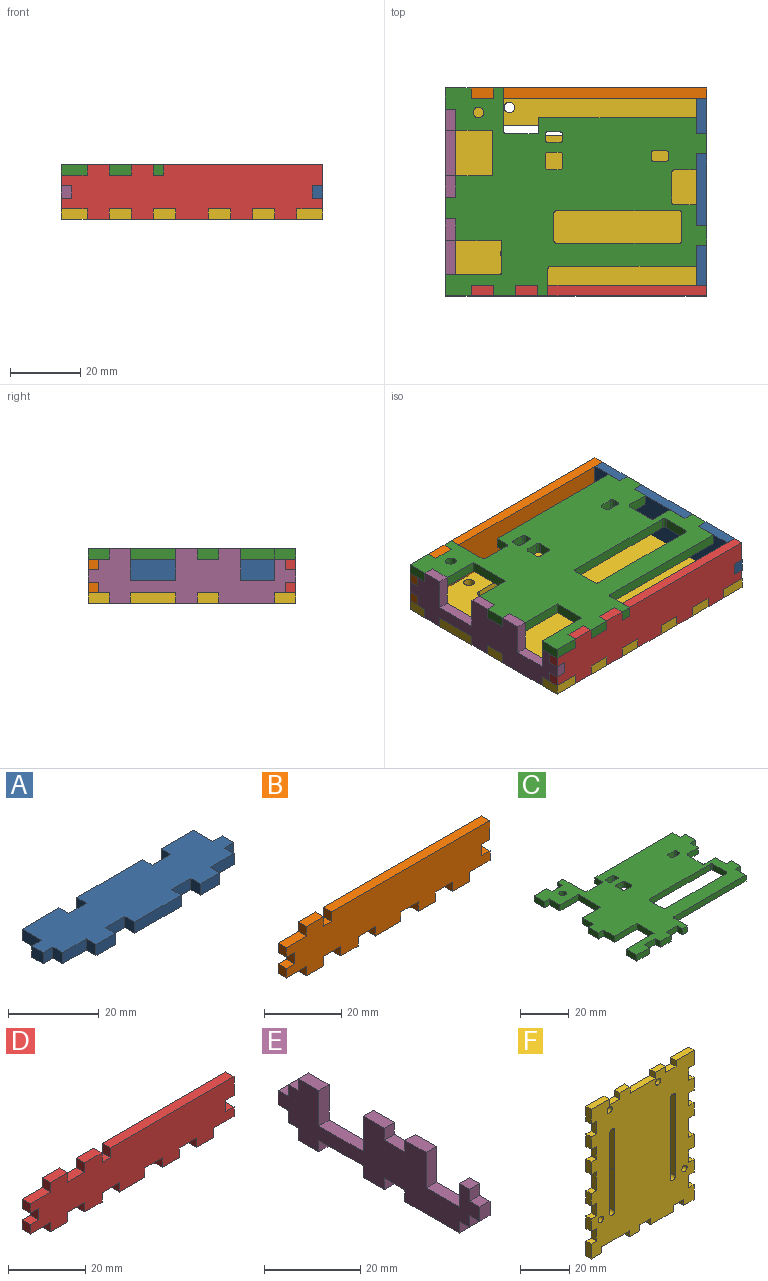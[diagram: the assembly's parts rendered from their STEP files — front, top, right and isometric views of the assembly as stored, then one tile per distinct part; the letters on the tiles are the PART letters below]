
ASSEMBLY  parts=6 mates=5
PART A: 34 faces, bbox 59.3x15.6x3 mm
  f0: plane 11.5x3mm, normal (0,1,0), area 34.5mm2, adj f1,f31,f32,f33
  f1: plane 6x3mm, normal (-1,0,0), area 18mm2, adj f0,f2,f32,f33
  f2: plane 3x3mm, normal (0,1,0), area 9mm2, adj f1,f3,f32,f33
  f3: plane 3.6x3mm, normal (-1,0,0), area 10.8mm2, adj f2,f4,f32,f33
  f4: plane 3x3mm, normal (0,-1,0), area 9mm2, adj f3,f5,f32,f33
  f5: plane 3x3mm, normal (-1,0,0), area 9mm2, adj f4,f6,f32,f33
  f6: plane 7.4x3mm, normal (0,-1,0), area 22.2mm2, adj f5,f7,f32,f33
  f7: plane 3x3mm, normal (-1,0,0), area 9mm2, adj f6,f8,f32,f33
  f8: plane 6x3mm, normal (0,-1,0), area 18mm2, adj f7,f9,f32,f33
  f9: plane 3x3mm, normal (1,0,0), area 9mm2, adj f8,f10,f32,f33
  f10: plane 6x3mm, normal (0,-1,0), area 18mm2, adj f9,f11,f32,f33
  f11: plane 3x3mm, normal (-1,0,0), area 9mm2, adj f10,f12,f32,f33
  f12: plane 14.5x3mm, normal (0,-1,0), area 43.5mm2, adj f11,f13,f32,f33
  f13: plane 3x3mm, normal (1,0,0), area 9mm2, adj f12,f14,f32,f33
  f14: plane 6x3mm, normal (0,-1,0), area 18mm2, adj f13,f15,f32,f33
  f15: plane 3x3mm, normal (-1,0,0), area 9mm2, adj f14,f16,f32,f33
  f16: plane 6x3mm, normal (0,-1,0), area 18mm2, adj f15,f17,f32,f33
  f17: plane 3x3mm, normal (1,0,0), area 9mm2, adj f16,f18,f32,f33
  f18: plane 7.4x3mm, normal (0,-1,0), area 22.2mm2, adj f17,f19,f32,f33
  f19: plane 3x3mm, normal (1,0,0), area 9mm2, adj f18,f20,f32,f33
  f20: plane 3x3mm, normal (0,-1,0), area 9mm2, adj f19,f21,f32,f33
  f21: plane 3.6x3mm, normal (1,0,0), area 10.8mm2, adj f20,f22,f32,f33
  f22: plane 3x3mm, normal (0,1,0), area 9mm2, adj f21,f23,f32,f33
  f23: plane 6x3mm, normal (1,0,0), area 18mm2, adj f22,f24,f32,f33
  f24: plane 10x3mm, normal (0,1,0), area 30mm2, adj f23,f25,f32,f33
  f25: plane 3x3mm, normal (-1,0,0), area 9mm2, adj f24,f26,f32,f33
  f26: plane 5.8x3mm, normal (0,1,0), area 17.4mm2, adj f25,f27,f32,f33
  f27: plane 3x3mm, normal (1,0,0), area 9mm2, adj f26,f28,f32,f33
  f28: plane 20.5x3mm, normal (0,1,0), area 61.5mm2, adj f27,f29,f32,f33
  f29: plane 3x3mm, normal (-1,0,0), area 9mm2, adj f28,f30,f32,f33
  f30: plane 5.5x3mm, normal (0,1,0), area 16.5mm2, adj f29,f31,f32,f33
  f31: plane 3x3mm, normal (1,0,0), area 9mm2, adj f0,f30,f32,f33
  f32: plane 59.3x15.6mm, normal (0,0,-1), area 738.8mm2, adj f0,f1,f2,f3,f4,f5,f6,f7
  f33: plane 59.3x15.6mm, normal (0,0,1), area 738.8mm2, adj f0,f1,f2,f3,f4,f5,f6,f7
PART B: 40 faces, bbox 74.6x3x15.6 mm
  f0: plane 3x3mm, normal (0,0,-1), area 9mm2, adj f1,f37,f38,f39
  f1: plane 6x3mm, normal (1,0,0), area 18mm2, adj f0,f2,f38,f39
  f2: plane 57.9x3mm, normal (0,0,1), area 173.7mm2, adj f1,f3,f38,f39
  f3: plane 3x3mm, normal (-1,0,0), area 9mm2, adj f2,f4,f38,f39
  f4: plane 3x3mm, normal (0,0,1), area 9mm2, adj f3,f5,f38,f39
  f5: plane 3x3mm, normal (1,0,0), area 9mm2, adj f4,f6,f38,f39
  f6: plane 6.3x3mm, normal (0,0,1), area 18.9mm2, adj f5,f7,f38,f39
  f7: plane 3x3mm, normal (-1,0,0), area 9mm2, adj f6,f8,f38,f39
  f8: plane 7.4x3mm, normal (0,0,1), area 22.2mm2, adj f7,f9,f38,f39
  f9: plane 3x3mm, normal (-1,0,0), area 9mm2, adj f8,f10,f38,f39
  f10: plane 3x3mm, normal (0,0,-1), area 9mm2, adj f9,f11,f38,f39
  f11: plane 3.6x3mm, normal (-1,0,0), area 10.8mm2, adj f10,f12,f38,f39
  f12: plane 3x3mm, normal (0,0,1), area 9mm2, adj f11,f13,f38,f39
  f13: plane 3x3mm, normal (-1,0,0), area 9mm2, adj f12,f14,f38,f39
  f14: plane 7.4x3mm, normal (0,0,-1), area 22.2mm2, adj f13,f15,f38,f39
  f15: plane 3x3mm, normal (-1,0,0), area 9mm2, adj f14,f16,f38,f39
  f16: plane 6.3x3mm, normal (0,0,-1), area 18.9mm2, adj f15,f17,f38,f39
  f17: plane 3x3mm, normal (1,0,0), area 9mm2, adj f16,f18,f38,f39
  f18: plane 6.3x3mm, normal (0,0,-1), area 18.9mm2, adj f17,f19,f38,f39
  f19: plane 3x3mm, normal (-1,0,0), area 9mm2, adj f18,f20,f38,f39
  f20: plane 6.3x3mm, normal (0,0,-1), area 18.9mm2, adj f19,f21,f38,f39
  f21: plane 3x3mm, normal (1,0,0), area 9mm2, adj f20,f22,f38,f39
  f22: plane 6.3x3mm, normal (0,0,-1), area 18.9mm2, adj f21,f23,f38,f39
  f23: plane 3x3mm, normal (-1,0,0), area 9mm2, adj f22,f24,f38,f39
  f24: plane 9.4x3mm, normal (0,0,-1), area 28.2mm2, adj f23,f25,f38,f39
  f25: plane 3x3mm, normal (1,0,0), area 9mm2, adj f24,f26,f38,f39
  f26: plane 6.3x3mm, normal (0,0,-1), area 18.9mm2, adj f25,f27,f38,f39
  f27: plane 3x3mm, normal (-1,0,0), area 9mm2, adj f26,f28,f38,f39
  f28: plane 6.3x3mm, normal (0,0,-1), area 18.9mm2, adj f27,f29,f38,f39
  f29: plane 3x3mm, normal (1,0,0), area 9mm2, adj f28,f30,f38,f39
  f30: plane 6.3x3mm, normal (0,0,-1), area 18.9mm2, adj f29,f31,f38,f39
  f31: plane 3x3mm, normal (-1,0,0), area 9mm2, adj f30,f32,f38,f39
  f32: plane 6.3x3mm, normal (0,0,-1), area 18.9mm2, adj f31,f33,f38,f39
  f33: plane 3x3mm, normal (1,0,0), area 9mm2, adj f32,f34,f38,f39
  f34: plane 7.4x3mm, normal (0,0,-1), area 22.2mm2, adj f33,f35,f38,f39
  f35: plane 3x3mm, normal (1,0,0), area 9mm2, adj f34,f36,f38,f39
  f36: plane 3x3mm, normal (0,0,1), area 9mm2, adj f35,f37,f38,f39
  f37: plane 3.6x3mm, normal (1,0,0), area 10.8mm2, adj f0,f36,f38,f39
  f38: plane 74.6x15.6mm, normal (0,-1,0), area 991mm2, adj f0,f1,f2,f3,f4,f5,f6,f7
  f39: plane 74.6x15.6mm, normal (0,1,0), area 991mm2, adj f0,f1,f2,f3,f4,f5,f6,f7
PART C: 88 faces, bbox 74.6x59.3x3 mm
  f0: plane 3x3mm, normal (0,1,0), area 9mm2, adj f1,f85,f86,f87
  f1: plane 6x3mm, normal (1,0,0), area 18mm2, adj f0,f2,f86,f87
  f2: plane 6.25x3mm, normal (0,1,0), area 18.7mm2, adj f1,f3,f86,f87
  f3: cylinder r=0.75mm len=3mm, axis (0,0,1), area 3.5mm2, adj f2,f4,f86,f87
  f4: plane 8.5x3mm, normal (1,0,0), area 25.5mm2, adj f3,f5,f86,f87
  f5: cylinder r=0.75mm len=3mm, axis (0,0,1), area 3.5mm2, adj f4,f6,f86,f87
  f6: plane 6.25x3mm, normal (0,-1,0), area 18.7mm2, adj f5,f7,f86,f87
  f7: plane 4.5x3mm, normal (1,0,0), area 13.5mm2, adj f6,f8,f86,f87
  f8: plane 3x3mm, normal (0,-1,0), area 9mm2, adj f7,f9,f86,f87
  f9: plane 5.8x3mm, normal (1,0,0), area 17.4mm2, adj f8,f10,f86,f87
  f10: plane 3x3mm, normal (0,1,0), area 9mm2, adj f9,f11,f86,f87
  f11: plane 4.5x3mm, normal (1,0,0), area 13.5mm2, adj f10,f12,f86,f87
  f12: plane 44.9x3mm, normal (0,1,0), area 134.7mm2, adj f11,f13,f86,f87
  f13: plane 3.85x3mm, normal (-1,0,0), area 11.5mm2, adj f12,f14,f86,f87
  f14: cylinder r=0.75mm len=3mm, axis (0,0,1), area 3.5mm2, adj f13,f15,f86,f87
  f15: plane 8.5x3mm, normal (0,1,0), area 25.5mm2, adj f14,f16,f86,f87
  f16: cylinder r=0.75mm len=3mm, axis (0,0,1), area 3.5mm2, adj f15,f17,f86,f87
  f17: plane 12.35x3mm, normal (1,0,0), area 37mm2, adj f16,f18,f86,f87
  f18: plane 3x3mm, normal (0,1,0), area 9mm2, adj f17,f19,f86,f87
  f19: plane 3x3mm, normal (-1,0,0), area 9mm2, adj f18,f20,f86,f87
  f20: plane 6.3x3mm, normal (0,1,0), area 18.9mm2, adj f19,f21,f86,f87
  f21: plane 3x3mm, normal (1,0,0), area 9mm2, adj f20,f22,f86,f87
  f22: plane 7.4x3mm, normal (0,1,0), area 22.2mm2, adj f21,f23,f86,f87
  f23: plane 6x3mm, normal (-1,0,0), area 18mm2, adj f22,f24,f86,f87
  f24: plane 3x3mm, normal (0,-1,0), area 9mm2, adj f23,f25,f86,f87
  f25: plane 6x3mm, normal (-1,0,0), area 18mm2, adj f24,f26,f86,f87
  f26: plane 10.5x3mm, normal (0,-1,0), area 31.5mm2, adj f25,f27,f86,f87
  f27: plane 13x3mm, normal (-1,0,0), area 39mm2, adj f26,f28,f86,f87
  f28: plane 10.5x3mm, normal (0,1,0), area 31.5mm2, adj f27,f29,f86,f87
  f29: plane 6.2x3mm, normal (-1,0,0), area 18.6mm2, adj f28,f30,f86,f87
  f30: plane 3x3mm, normal (0,1,0), area 9mm2, adj f29,f31,f86,f87
  f31: plane 6.1x3mm, normal (-1,0,0), area 18.3mm2, adj f30,f32,f86,f87
  f32: plane 3x3mm, normal (0,-1,0), area 9mm2, adj f31,f33,f86,f87
  f33: plane 6.2x3mm, normal (-1,0,0), area 18.6mm2, adj f32,f34,f86,f87
  f34: plane 13x3mm, normal (0,-1,0), area 39mm2, adj f33,f35,f86,f87
  f35: plane 9.8x3mm, normal (-1,0,0), area 29.4mm2, adj f34,f36,f86,f87
  f36: plane 16x3mm, normal (0,1,0), area 48mm2, adj f35,f37,f86,f87
  f37: plane 6x3mm, normal (-1,0,0), area 18mm2, adj f36,f38,f86,f87
  f38: plane 7.4x3mm, normal (0,-1,0), area 22.2mm2, adj f37,f39,f86,f87
  f39: plane 3x3mm, normal (1,0,0), area 9mm2, adj f38,f40,f86,f87
  f40: plane 6.3x3mm, normal (0,-1,0), area 18.9mm2, adj f39,f41,f86,f87
  f41: plane 3x3mm, normal (-1,0,0), area 9mm2, adj f40,f42,f86,f87
  f42: plane 6.3x3mm, normal (0,-1,0), area 18.9mm2, adj f41,f43,f86,f87
  f43: plane 3x3mm, normal (1,0,0), area 9mm2, adj f42,f44,f86,f87
  f44: plane 6.3x3mm, normal (0,-1,0), area 18.9mm2, adj f43,f45,f86,f87
  f45: plane 3x3mm, normal (-1,0,0), area 9mm2, adj f44,f46,f86,f87
  f46: plane 3x3mm, normal (0,-1,0), area 9mm2, adj f45,f47,f86,f87
  f47: plane 7.75x3mm, normal (1,0,0), area 23.2mm2, adj f46,f48,f86,f87
  f48: cylinder r=0.75mm len=3mm, axis (0,0,1), area 3.5mm2, adj f47,f49,f86,f87
  f49: plane 41.55x3mm, normal (0,-1,0), area 124.6mm2, adj f48,f50,f86,f87
  f50: plane 6x3mm, normal (1,0,0), area 18mm2, adj f49,f51,f86,f87
  f51: plane 3x3mm, normal (0,-1,0), area 9mm2, adj f50,f85,f86,f87
  f52: cylinder r=0.75mm len=3mm, axis (0,0,1), area 3.5mm2, adj f53,f81,f86,f87
  f53: plane 3x1.5mm, normal (-1,0,0), area 4.5mm2, adj f52,f54,f86,f87
  f54: cylinder r=0.75mm len=3mm, axis (0,0,1), area 3.5mm2, adj f53,f55,f86,f87
  f55: plane 3.5x3mm, normal (0,1,0), area 10.5mm2, adj f54,f56,f86,f87
  f56: cylinder r=0.75mm len=3mm, axis (0,0,1), area 3.5mm2, adj f55,f57,f86,f87
  f57: plane 3x1.5mm, normal (1,0,0), area 4.5mm2, adj f56,f58,f86,f87
  f58: cylinder r=0.75mm len=3mm, axis (0,0,1), area 3.5mm2, adj f57,f81,f86,f87
  f59: cylinder r=0.75mm len=3mm, axis (0,0,1), area 3.5mm2, adj f60,f82,f86,f87
  f60: plane 3.5x3mm, normal (0,-1,0), area 10.5mm2, adj f59,f61,f86,f87
  f61: cylinder r=0.75mm len=3mm, axis (0,0,1), area 3.5mm2, adj f60,f62,f86,f87
  f62: plane 3x1.5mm, normal (-1,0,0), area 4.5mm2, adj f61,f63,f86,f87
  f63: cylinder r=0.75mm len=3mm, axis (0,0,1), area 3.5mm2, adj f62,f64,f86,f87
  f64: plane 3.5x3mm, normal (0,1,0), area 10.5mm2, adj f63,f65,f86,f87
  f65: cylinder r=0.75mm len=3mm, axis (0,0,1), area 3.5mm2, adj f64,f82,f86,f87
  f66: cylinder r=0.75mm len=3mm, axis (0,0,1), area 3.5mm2, adj f67,f83,f86,f87
  f67: plane 3.5x3mm, normal (0,-1,0), area 10.5mm2, adj f66,f68,f86,f87
  f68: cylinder r=0.75mm len=3mm, axis (0,0,1), area 3.5mm2, adj f67,f69,f86,f87
  f69: plane 3.5x3mm, normal (-1,0,0), area 10.5mm2, adj f68,f70,f86,f87
  f70: cylinder r=0.75mm len=3mm, axis (0,0,1), area 3.5mm2, adj f69,f71,f86,f87
  f71: plane 3.5x3mm, normal (0,1,0), area 10.5mm2, adj f70,f72,f86,f87
  f72: cylinder r=0.75mm len=3mm, axis (0,0,1), area 3.5mm2, adj f71,f83,f86,f87
  f73: cylinder r=0.75mm len=3mm, axis (0,0,1), area 3.5mm2, adj f74,f84,f86,f87
  f74: plane 35x3mm, normal (0,-1,0), area 105mm2, adj f73,f75,f86,f87
  f75: cylinder r=0.75mm len=3mm, axis (0,0,1), area 3.5mm2, adj f74,f76,f86,f87
  f76: plane 7.8x3mm, normal (-1,0,0), area 23.4mm2, adj f75,f77,f86,f87
  f77: cylinder r=0.75mm len=3mm, axis (0,0,1), area 3.5mm2, adj f76,f78,f86,f87
  f78: plane 35x3mm, normal (0,1,0), area 105mm2, adj f77,f79,f86,f87
  f79: cylinder r=0.75mm len=3mm, axis (0,0,1), area 3.5mm2, adj f78,f84,f86,f87
  f80: cylinder r=1.5mm len=3mm, axis (0,0,1), area 28.3mm2, adj f86,f87
  f81: plane 3.5x3mm, normal (0,-1,0), area 10.5mm2, adj f52,f58,f86,f87
  f82: plane 3x1.5mm, normal (1,0,0), area 4.5mm2, adj f59,f65,f86,f87
  f83: plane 3.5x3mm, normal (1,0,0), area 10.5mm2, adj f66,f72,f86,f87
  f84: plane 7.8x3mm, normal (1,0,0), area 23.4mm2, adj f73,f79,f86,f87
  f85: plane 5.5x3mm, normal (1,0,0), area 16.5mm2, adj f0,f51,f86,f87
  f86: plane 74.6x59.3mm, normal (0,0,-1), area 2494.4mm2, adj f0,f1,f2,f3,f4,f5,f6,f7
  f87: plane 74.6x59.3mm, normal (0,0,1), area 2494.4mm2, adj f0,f1,f2,f3,f4,f5,f6,f7
PART D: 44 faces, bbox 74.6x3x15.6 mm
  f0: plane 3x3mm, normal (1,0,0), area 9mm2, adj f1,f41,f42,f43
  f1: plane 6.3x3mm, normal (0,0,-1), area 18.9mm2, adj f0,f2,f42,f43
  f2: plane 3x3mm, normal (-1,0,0), area 9mm2, adj f1,f3,f42,f43
  f3: plane 9.4x3mm, normal (0,0,-1), area 28.2mm2, adj f2,f4,f42,f43
  f4: plane 3x3mm, normal (1,0,0), area 9mm2, adj f3,f5,f42,f43
  f5: plane 6.3x3mm, normal (0,0,-1), area 18.9mm2, adj f4,f6,f42,f43
  f6: plane 3x3mm, normal (-1,0,0), area 9mm2, adj f5,f7,f42,f43
  f7: plane 6.3x3mm, normal (0,0,-1), area 18.9mm2, adj f6,f8,f42,f43
  f8: plane 3x3mm, normal (1,0,0), area 9mm2, adj f7,f9,f42,f43
  f9: plane 6.3x3mm, normal (0,0,-1), area 18.9mm2, adj f8,f10,f42,f43
  f10: plane 3x3mm, normal (-1,0,0), area 9mm2, adj f9,f11,f42,f43
  f11: plane 6.3x3mm, normal (0,0,-1), area 18.9mm2, adj f10,f12,f42,f43
  f12: plane 3x3mm, normal (1,0,0), area 9mm2, adj f11,f13,f42,f43
  f13: plane 7.4x3mm, normal (0,0,-1), area 22.2mm2, adj f12,f14,f42,f43
  f14: plane 3x3mm, normal (1,0,0), area 9mm2, adj f13,f15,f42,f43
  f15: plane 3x3mm, normal (0,0,1), area 9mm2, adj f14,f16,f42,f43
  f16: plane 3.6x3mm, normal (1,0,0), area 10.8mm2, adj f15,f17,f42,f43
  f17: plane 3x3mm, normal (0,0,-1), area 9mm2, adj f16,f18,f42,f43
  f18: plane 6x3mm, normal (1,0,0), area 18mm2, adj f17,f19,f42,f43
  f19: plane 45.3x3mm, normal (0,0,1), area 135.9mm2, adj f18,f20,f42,f43
  f20: plane 3x3mm, normal (-1,0,0), area 9mm2, adj f19,f21,f42,f43
  f21: plane 3x3mm, normal (0,0,1), area 9mm2, adj f20,f22,f42,f43
  f22: plane 3x3mm, normal (1,0,0), area 9mm2, adj f21,f23,f42,f43
  f23: plane 6.3x3mm, normal (0,0,1), area 18.9mm2, adj f22,f24,f42,f43
  f24: plane 3x3mm, normal (-1,0,0), area 9mm2, adj f23,f25,f42,f43
  f25: plane 6.3x3mm, normal (0,0,1), area 18.9mm2, adj f24,f26,f42,f43
  f26: plane 3x3mm, normal (1,0,0), area 9mm2, adj f25,f27,f42,f43
  f27: plane 6.3x3mm, normal (0,0,1), area 18.9mm2, adj f26,f28,f42,f43
  f28: plane 3x3mm, normal (-1,0,0), area 9mm2, adj f27,f29,f42,f43
  f29: plane 7.4x3mm, normal (0,0,1), area 22.2mm2, adj f28,f30,f42,f43
  f30: plane 3x3mm, normal (-1,0,0), area 9mm2, adj f29,f31,f42,f43
  f31: plane 3x3mm, normal (0,0,-1), area 9mm2, adj f30,f32,f42,f43
  f32: plane 3.6x3mm, normal (-1,0,0), area 10.8mm2, adj f31,f33,f42,f43
  f33: plane 3x3mm, normal (0,0,1), area 9mm2, adj f32,f34,f42,f43
  f34: plane 3x3mm, normal (-1,0,0), area 9mm2, adj f33,f35,f42,f43
  f35: plane 7.4x3mm, normal (0,0,-1), area 22.2mm2, adj f34,f36,f42,f43
  f36: plane 3x3mm, normal (-1,0,0), area 9mm2, adj f35,f37,f42,f43
  f37: plane 6.3x3mm, normal (0,0,-1), area 18.9mm2, adj f36,f38,f42,f43
  f38: plane 3x3mm, normal (1,0,0), area 9mm2, adj f37,f39,f42,f43
  f39: plane 6.3x3mm, normal (0,0,-1), area 18.9mm2, adj f38,f40,f42,f43
  f40: plane 3x3mm, normal (-1,0,0), area 9mm2, adj f39,f41,f42,f43
  f41: plane 6.3x3mm, normal (0,0,-1), area 18.9mm2, adj f0,f40,f42,f43
  f42: plane 74.6x15.6mm, normal (0,1,0), area 972.1mm2, adj f0,f1,f2,f3,f4,f5,f6,f7
  f43: plane 74.6x15.6mm, normal (0,-1,0), area 972.1mm2, adj f0,f1,f2,f3,f4,f5,f6,f7
PART E: 40 faces, bbox 3x59.3x15.6 mm
  f0: plane 3x3mm, normal (0,0,1), area 9mm2, adj f1,f37,f38,f39
  f1: plane 3.6x3mm, normal (0,-1,0), area 10.8mm2, adj f0,f2,f38,f39
  f2: plane 3x3mm, normal (0,0,-1), area 9mm2, adj f1,f3,f38,f39
  f3: plane 3x3mm, normal (0,-1,0), area 9mm2, adj f2,f4,f38,f39
  f4: plane 3x3mm, normal (0,0,-1), area 9mm2, adj f3,f5,f38,f39
  f5: plane 3x3mm, normal (0,-1,0), area 9mm2, adj f4,f6,f38,f39
  f6: plane 16x3mm, normal (0,0,-1), area 48mm2, adj f5,f7,f38,f39
  f7: plane 3x3mm, normal (0,1,0), area 9mm2, adj f6,f8,f38,f39
  f8: plane 6.1x3mm, normal (0,0,-1), area 18.3mm2, adj f7,f9,f38,f39
  f9: plane 3x3mm, normal (0,-1,0), area 9mm2, adj f8,f10,f38,f39
  f10: plane 6.2x3mm, normal (0,0,-1), area 18.6mm2, adj f9,f11,f38,f39
  f11: plane 3x3mm, normal (0,1,0), area 9mm2, adj f10,f12,f38,f39
  f12: plane 13x3mm, normal (0,0,-1), area 39mm2, adj f11,f13,f38,f39
  f13: plane 3x3mm, normal (0,-1,0), area 9mm2, adj f12,f14,f38,f39
  f14: plane 6x3mm, normal (0,0,-1), area 18mm2, adj f13,f15,f38,f39
  f15: plane 3x3mm, normal (0,1,0), area 9mm2, adj f14,f16,f38,f39
  f16: plane 3x3mm, normal (0,0,-1), area 9mm2, adj f15,f17,f38,f39
  f17: plane 3x3mm, normal (0,1,0), area 9mm2, adj f16,f18,f38,f39
  f18: plane 3x3mm, normal (0,0,-1), area 9mm2, adj f17,f19,f38,f39
  f19: plane 3.6x3mm, normal (0,1,0), area 10.8mm2, adj f18,f20,f38,f39
  f20: plane 3x3mm, normal (0,0,1), area 9mm2, adj f19,f21,f38,f39
  f21: plane 3x3mm, normal (0,1,0), area 9mm2, adj f20,f22,f38,f39
  f22: plane 3x3mm, normal (0,0,1), area 9mm2, adj f21,f23,f38,f39
  f23: plane 3x3mm, normal (0,1,0), area 9mm2, adj f22,f24,f38,f39
  f24: plane 6x3mm, normal (0,0,1), area 18mm2, adj f23,f25,f38,f39
  f25: plane 9x3mm, normal (0,-1,0), area 27mm2, adj f24,f26,f38,f39
  f26: plane 13x3mm, normal (0,0,1), area 39mm2, adj f25,f27,f38,f39
  f27: plane 9x3mm, normal (0,1,0), area 27mm2, adj f26,f28,f38,f39
  f28: plane 6.2x3mm, normal (0,0,1), area 18.6mm2, adj f27,f29,f38,f39
  f29: plane 3x3mm, normal (0,-1,0), area 9mm2, adj f28,f30,f38,f39
  f30: plane 6.1x3mm, normal (0,0,1), area 18.3mm2, adj f29,f31,f38,f39
  f31: plane 3x3mm, normal (0,1,0), area 9mm2, adj f30,f32,f38,f39
  f32: plane 6.2x3mm, normal (0,0,1), area 18.6mm2, adj f31,f33,f38,f39
  f33: plane 9x3mm, normal (0,-1,0), area 27mm2, adj f32,f34,f38,f39
  f34: plane 9.8x3mm, normal (0,0,1), area 29.4mm2, adj f33,f35,f38,f39
  f35: plane 6x3mm, normal (0,1,0), area 18mm2, adj f34,f36,f38,f39
  f36: plane 3x3mm, normal (0,0,1), area 9mm2, adj f35,f37,f38,f39
  f37: plane 3x3mm, normal (0,-1,0), area 9mm2, adj f0,f36,f38,f39
  f38: plane 59.3x15.6mm, normal (1,0,0), area 536.3mm2, adj f0,f1,f2,f3,f4,f5,f6,f7
  f39: plane 59.3x15.6mm, normal (-1,0,0), area 536.3mm2, adj f0,f1,f2,f3,f4,f5,f6,f7
PART F: 83 faces, bbox 59.3x3x74.6 mm
  f0: cylinder r=1.5mm len=3mm, axis (0,-1,0), area 14.2mm2, adj f1,f80,f81,f82
  f1: plane 39.98x3mm, normal (-1,0,0), area 119.9mm2, adj f0,f2,f81,f82
  f2: cylinder r=1.5mm len=3mm, axis (0,-1,0), area 14.2mm2, adj f1,f80,f81,f82
  f3: plane 20x3mm, normal (-1,0,0), area 60mm2, adj f4,f74,f81,f82
  f4: cylinder r=1.5mm len=3mm, axis (0,-1,0), area 14.2mm2, adj f3,f5,f81,f82
  f5: plane 39.99x3mm, normal (1,0,0), area 120mm2, adj f4,f6,f81,f82
  f6: cylinder r=1.5mm len=3mm, axis (0,-1,0), area 14.1mm2, adj f5,f74,f81,f82
  f7: plane 9.4x3mm, normal (1,0,0), area 28.2mm2, adj f8,f75,f81,f82
  f8: plane 3x3mm, normal (0,0,-1), area 9mm2, adj f7,f9,f81,f82
  f9: plane 6.3x3mm, normal (1,0,0), area 18.9mm2, adj f8,f10,f81,f82
  f10: plane 3x3mm, normal (0,0,1), area 9mm2, adj f9,f11,f81,f82
  f11: plane 6.3x3mm, normal (1,0,0), area 18.9mm2, adj f10,f12,f81,f82
  f12: plane 3x3mm, normal (0,0,-1), area 9mm2, adj f11,f13,f81,f82
  f13: plane 6.3x3mm, normal (1,0,0), area 18.9mm2, adj f12,f14,f81,f82
  f14: plane 3x3mm, normal (0,0,1), area 9mm2, adj f13,f15,f81,f82
  f15: plane 6.3x3mm, normal (1,0,0), area 18.9mm2, adj f14,f16,f81,f82
  f16: plane 3x3mm, normal (0,0,-1), area 9mm2, adj f15,f17,f81,f82
  f17: plane 7.4x3mm, normal (1,0,0), area 22.2mm2, adj f16,f18,f81,f82
  f18: plane 10.4x3mm, normal (0,0,1), area 31.2mm2, adj f17,f19,f81,f82
  f19: plane 3x3mm, normal (-1,0,0), area 9mm2, adj f18,f20,f81,f82
  f20: plane 6x3mm, normal (0,0,1), area 18mm2, adj f19,f21,f81,f82
  f21: plane 3x3mm, normal (1,0,0), area 9mm2, adj f20,f22,f81,f82
  f22: plane 6x3mm, normal (0,0,1), area 18mm2, adj f21,f23,f81,f82
  f23: plane 3x3mm, normal (-1,0,0), area 9mm2, adj f22,f24,f81,f82
  f24: plane 14.5x3mm, normal (0,0,1), area 43.5mm2, adj f23,f25,f81,f82
  f25: plane 3x3mm, normal (1,0,0), area 9mm2, adj f24,f26,f81,f82
  f26: plane 6x3mm, normal (0,0,1), area 18mm2, adj f25,f27,f81,f82
  f27: plane 3x3mm, normal (-1,0,0), area 9mm2, adj f26,f28,f81,f82
  f28: plane 6x3mm, normal (0,0,1), area 18mm2, adj f27,f29,f81,f82
  f29: plane 3x3mm, normal (1,0,0), area 9mm2, adj f28,f30,f81,f82
  f30: plane 10.4x3mm, normal (0,0,1), area 31.2mm2, adj f29,f31,f81,f82
  f31: plane 7.4x3mm, normal (-1,0,0), area 22.2mm2, adj f30,f32,f81,f82
  f32: plane 3x3mm, normal (0,0,-1), area 9mm2, adj f31,f33,f81,f82
  f33: plane 6.3x3mm, normal (-1,0,0), area 18.9mm2, adj f32,f34,f81,f82
  f34: plane 3x3mm, normal (0,0,1), area 9mm2, adj f33,f35,f81,f82
  f35: plane 6.3x3mm, normal (-1,0,0), area 18.9mm2, adj f34,f36,f81,f82
  f36: plane 3x3mm, normal (0,0,-1), area 9mm2, adj f35,f37,f81,f82
  f37: plane 6.3x3mm, normal (-1,0,0), area 18.9mm2, adj f36,f38,f81,f82
  f38: plane 3x3mm, normal (0,0,1), area 9mm2, adj f37,f39,f81,f82
  f39: plane 6.3x3mm, normal (-1,0,0), area 18.9mm2, adj f38,f40,f81,f82
  f40: plane 3x3mm, normal (0,0,-1), area 9mm2, adj f39,f41,f81,f82
  f41: plane 9.4x3mm, normal (-1,0,0), area 28.2mm2, adj f40,f42,f81,f82
  f42: plane 3x3mm, normal (0,0,1), area 9mm2, adj f41,f43,f81,f82
  f43: plane 6.3x3mm, normal (-1,0,0), area 18.9mm2, adj f42,f44,f81,f82
  f44: plane 3x3mm, normal (0,0,-1), area 9mm2, adj f43,f45,f81,f82
  f45: plane 6.3x3mm, normal (-1,0,0), area 18.9mm2, adj f44,f46,f81,f82
  f46: plane 3x3mm, normal (0,0,1), area 9mm2, adj f45,f47,f81,f82
  f47: plane 6.3x3mm, normal (-1,0,0), area 18.9mm2, adj f46,f48,f81,f82
  f48: plane 3x3mm, normal (0,0,-1), area 9mm2, adj f47,f49,f81,f82
  f49: plane 6.3x3mm, normal (-1,0,0), area 18.9mm2, adj f48,f50,f81,f82
  f50: plane 3x3mm, normal (0,0,1), area 9mm2, adj f49,f51,f81,f82
  f51: plane 7.4x3mm, normal (-1,0,0), area 22.2mm2, adj f50,f52,f81,f82
  f52: plane 6x3mm, normal (0,0,-1), area 18mm2, adj f51,f53,f81,f82
  f53: plane 3x3mm, normal (1,0,0), area 9mm2, adj f52,f54,f81,f82
  f54: plane 16x3mm, normal (0,0,-1), area 48mm2, adj f53,f55,f81,f82
  f55: plane 3x3mm, normal (-1,0,0), area 9mm2, adj f54,f56,f81,f82
  f56: plane 6.1x3mm, normal (0,0,-1), area 18.3mm2, adj f55,f57,f81,f82
  f57: plane 3x3mm, normal (1,0,0), area 9mm2, adj f56,f58,f81,f82
  f58: plane 6.2x3mm, normal (0,0,-1), area 18.6mm2, adj f57,f59,f81,f82
  f59: plane 3x3mm, normal (-1,0,0), area 9mm2, adj f58,f60,f81,f82
  f60: plane 13x3mm, normal (0,0,-1), area 39mm2, adj f59,f61,f81,f82
  f61: plane 3x3mm, normal (1,0,0), area 9mm2, adj f60,f62,f81,f82
  f62: plane 6x3mm, normal (0,0,-1), area 18mm2, adj f61,f63,f81,f82
  f63: plane 3x3mm, normal (-1,0,0), area 9mm2, adj f62,f64,f81,f82
  f64: plane 6x3mm, normal (0,0,-1), area 18mm2, adj f63,f65,f81,f82
  f65: plane 7.4x3mm, normal (1,0,0), area 22.2mm2, adj f64,f66,f81,f82
  f66: plane 3x3mm, normal (0,0,1), area 9mm2, adj f65,f67,f81,f82
  f67: plane 6.3x3mm, normal (1,0,0), area 18.9mm2, adj f66,f68,f81,f82
  f68: plane 3x3mm, normal (0,0,-1), area 9mm2, adj f67,f69,f81,f82
  f69: plane 6.3x3mm, normal (1,0,0), area 18.9mm2, adj f68,f70,f81,f82
  f70: plane 3x3mm, normal (0,0,1), area 9mm2, adj f69,f71,f81,f82
  f71: plane 6.3x3mm, normal (1,0,0), area 18.9mm2, adj f70,f72,f81,f82
  f72: plane 3x3mm, normal (0,0,-1), area 9mm2, adj f71,f73,f81,f82
  f73: plane 6.3x3mm, normal (1,0,0), area 18.9mm2, adj f72,f75,f81,f82
  f74: plane 20x3mm, normal (-1,0,0), area 60mm2, adj f3,f6,f81,f82
  f75: plane 3x3mm, normal (0,0,1), area 9mm2, adj f7,f73,f81,f82
  f76: cylinder r=1.5mm len=3mm, axis (0,-1,0), area 28.3mm2, adj f81,f82
  f77: cylinder r=1.5mm len=3mm, axis (0,-1,0), area 28.3mm2, adj f81,f82
  f78: cylinder r=1.5mm len=3mm, axis (0,-1,0), area 28.3mm2, adj f81,f82
  f79: cylinder r=1.5mm len=3mm, axis (0,-1,0), area 28.3mm2, adj f81,f82
  f80: plane 40x3mm, normal (1,0,0), area 120mm2, adj f0,f2,f81,f82
  f81: plane 74.6x59.3mm, normal (0,1,0), area 3769.7mm2, adj f0,f1,f2,f3,f4,f5,f6,f7
  f82: plane 74.6x59.3mm, normal (0,-1,0), area 3769.7mm2, adj f0,f1,f2,f3,f4,f5,f6,f7
PLACE A rot(axis=(0.58,0.58,0.58),120deg) t=(74.6,0,0)mm
PLACE B t=(74.6,59.3,0)mm
PLACE C at identity fixed
PLACE D at identity
PLACE E at identity
PLACE F rot(axis=(0.58,0.58,0.58),120deg) t=(7.4,0,-15.6)mm
MATE fastened C.f23 <-> B.f9  axis (-1,0,0) through (0,59.3,-3)mm
MATE fastened C.f37 <-> D.f30  axis (1,0,0) through (0,0,-3)mm
MATE fastened D.f43 <-> E.f1  axis (0,-1,0) through (0,0,-6)mm
MATE fastened D.f43 <-> A.f3  axis (0,-1,0) through (74.6,0,-6)mm
MATE fastened F.f50 <-> D.f36  axis (1,0,0) through (7.4,0,-15.6)mm
